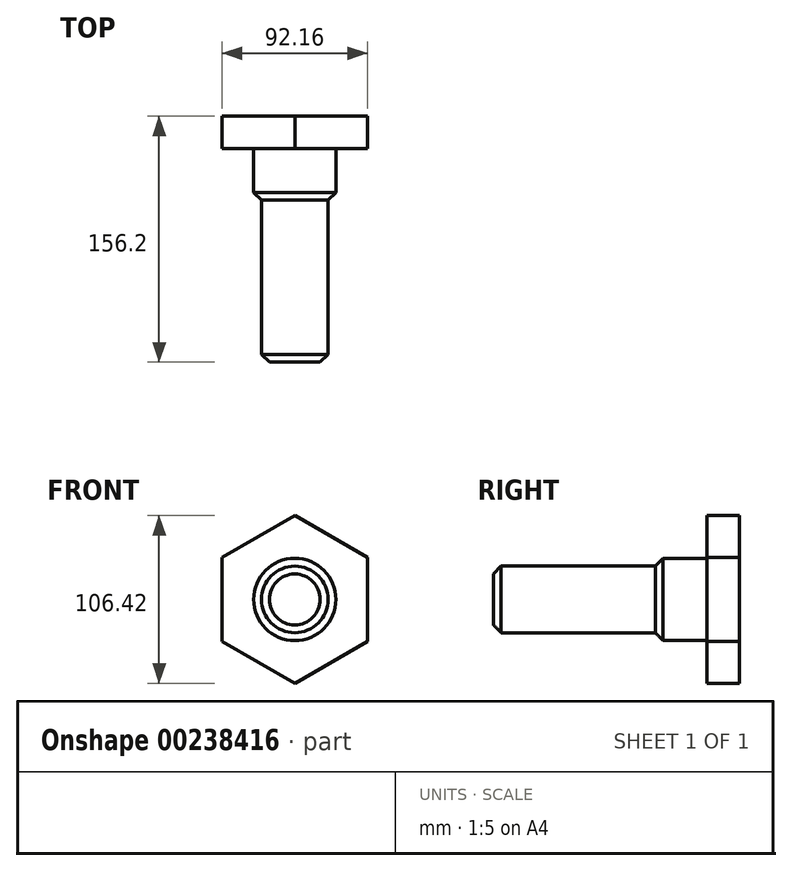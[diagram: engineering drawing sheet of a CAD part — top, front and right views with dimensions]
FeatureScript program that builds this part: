
annotation { "Feature Type Name" : "Feature", "Feature Type Description" : "" }
export const myFeature = defineFeature(function(context is Context, id is Id, definition is map)
    precondition{}
    {
        {
            var Q0;
            Q0=qCreatedBy(makeId("Front.planeOp"),FACE);
            var sketch = newSketch(context, id + "F0", { "sketchPlane" : qUnion([Q0])});
            skCircle(sketch, "E0.cCircle", {"center": v(0, 0) * mm, "radius": 46.08 * mm, "construction": true});
            skLineSegment(sketch, "E0.0", {"start": v(46.08, 26.6) * mm, "end": v(46.08, -26.6) * mm});
            skLineSegment(sketch, "E0.1", {"start": v(46.08, -26.6) * mm, "end": v(0, -53.2) * mm});
            skLineSegment(sketch, "E0.2", {"start": v(0, -53.2) * mm, "end": v(-46.08, -26.6) * mm});
            skLineSegment(sketch, "E0.3", {"start": v(-46.08, -26.6) * mm, "end": v(-46.08, 26.6) * mm});
            skLineSegment(sketch, "E0.4", {"start": v(-46.08, 26.6) * mm, "end": v(0, 53.2) * mm});
            skLineSegment(sketch, "E0.5", {"start": v(0, 53.2) * mm, "end": v(46.08, 26.6) * mm});
            skPoint(sketch, "E0.0.midPoint", {"position": v(46.08, 0) * mm});
            skSolve(sketch);
        }
        {
            var Q0;
            Q0 = qSketchRegion(id + "F0", true);
            extrude(context, id + "F1", {"entities" : qUnion([Q0]), "depth" : 20.5 * mm});
        }
        {
            var Q0;
            Q0=makeQuery(id+"F1.opExtrude","CAP_FACE",FACE,{"disambiguationData":[OSD([sQuery(id+"F0.wireOp",EDGE,"E0.0"),sQuery(id+"F0.wireOp",EDGE,"E0.1"),sQuery(id+"F0.wireOp",EDGE,"E0.2"),sQuery(id+"F0.wireOp",EDGE,"E0.3"),sQuery(id+"F0.wireOp",EDGE,"E0.4"),sQuery(id+"F0.wireOp",EDGE,"E0.5")])],"isStart":false});
            var sketch = newSketch(context, id + "F2", { "sketchPlane" : qUnion([Q0])});
            skCircle(sketch, "E1", {"center": v(0, 0) * mm, "radius": 26.14 * mm});
            skSolve(sketch);
        }
        {
            var Q0;
            Q0 = qSketchRegion(id + "F2", true);
            extrude(context, id + "F3", {"entities" : qUnion([Q0]), "operationType" : NewBodyOperationType.ADD, "depth" : 32.8 * mm});
        }
        {
            var Q0;
            Q0=makeQuery(id+"F3.opExtrude","CAP_EDGE",EDGE,{"disambiguationData":[OSD([sQuery(id+"F2.wireOp",EDGE,"E1")])],"isStart":false});
            chamfer(context, id + "F4", {"entities" : qUnion([Q0]), "width" : 5 * mm, "tangentPropagation" : true});
        }
        {
            var Q0;
            Q0=makeQuery(id+"F3.opExtrude","CAP_FACE",FACE,{"disambiguationData":[OSD([sQuery(id+"F2.wireOp",EDGE,"E1")])],"isStart":false});
            extrude(context, id + "F5", {"entities" : qUnion([Q0]), "operationType" : NewBodyOperationType.ADD, "depth" : 102.9 * mm});
        }
        {
            var Q0;
            Q0=makeQuery(id+"F5.opExtrude","CAP_EDGE",EDGE,{"disambiguationData":[OSD([sQuery(id+"F2.wireOp",EDGE,"E1")])],"isStart":false});
            chamfer(context, id + "F6", {"entities" : qUnion([Q0]), "width" : 5 * mm, "tangentPropagation" : true});
        }
    });
